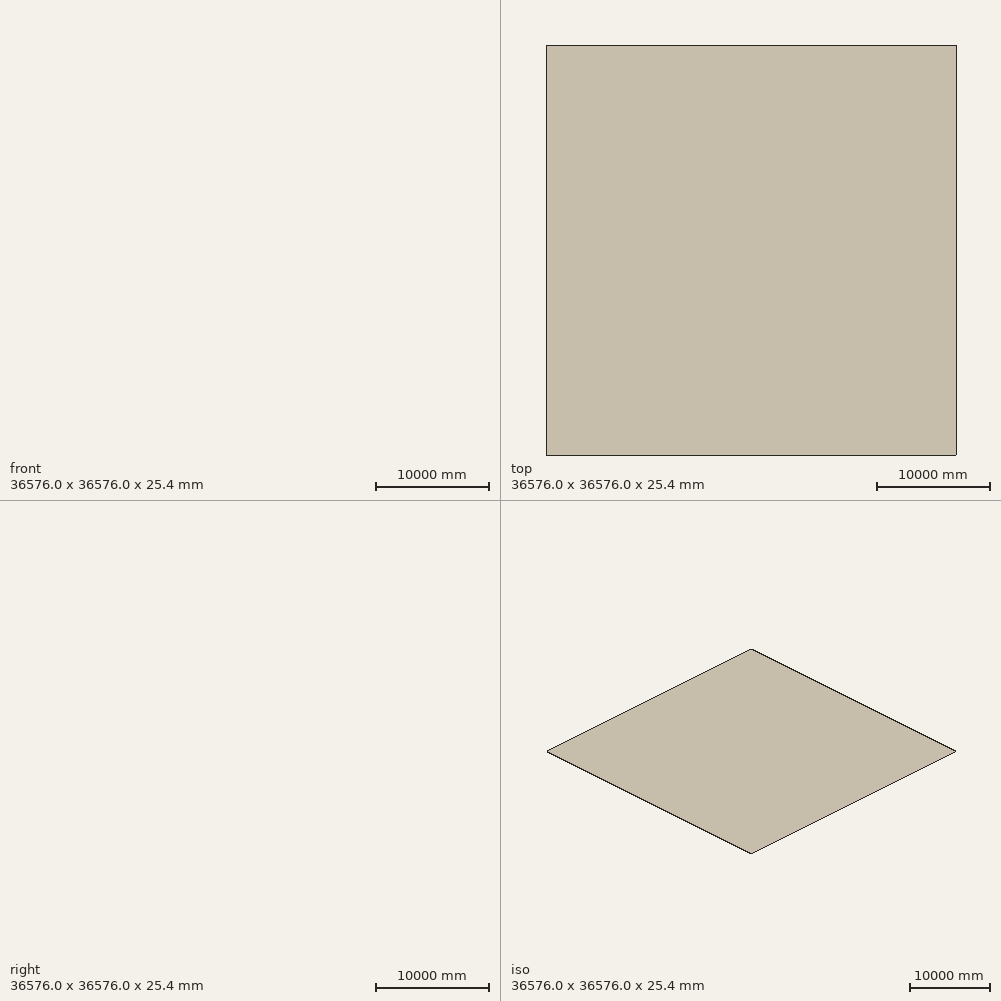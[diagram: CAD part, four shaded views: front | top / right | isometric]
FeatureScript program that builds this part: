
annotation { "Feature Type Name" : "Feature", "Feature Type Description" : "" }
export const myFeature = defineFeature(function(context is Context, id is Id, definition is map)
    precondition{}
    {
        {
            var Q0;
            Q0=qCreatedBy(makeId("Top.planeOp"),FACE);
            var sketch = newSketch(context, id + "F0", { "sketchPlane" : qUnion([Q0])});
            skLineSegment(sketch, "E0.bottom", {"start": v(-18288, 18288) * mm, "end": v(18288, 18288) * mm});
            skLineSegment(sketch, "E0.top", {"start": v(-18288, -18288) * mm, "end": v(18288, -18288) * mm});
            skLineSegment(sketch, "E0.left", {"start": v(-18288, 18288) * mm, "end": v(-18288, -18288) * mm});
            skLineSegment(sketch, "E0.right", {"start": v(18288, 18288) * mm, "end": v(18288, -18288) * mm});
            skPoint(sketch, "E0.middle", {"position": v(0, 0) * mm});
            skSolve(sketch);
        }
        {
            var Q0;
            Q0=makeQuery(id+"F0.imprint","IMPRINT",FACE,{"disambiguationData":[TD([[makeQuery(id+"F0.imprint","IMPRINT",EDGE,{"derivedFrom":sQuery(id+"F0.wireOp",EDGE,"E0.bottom")}),-1.0]])]});
            extrude(context, id + "F1", {"entities" : qUnion([Q0]), "oppositeDirection" : true, "depth" : 25.4 * mm});
        }
    });
